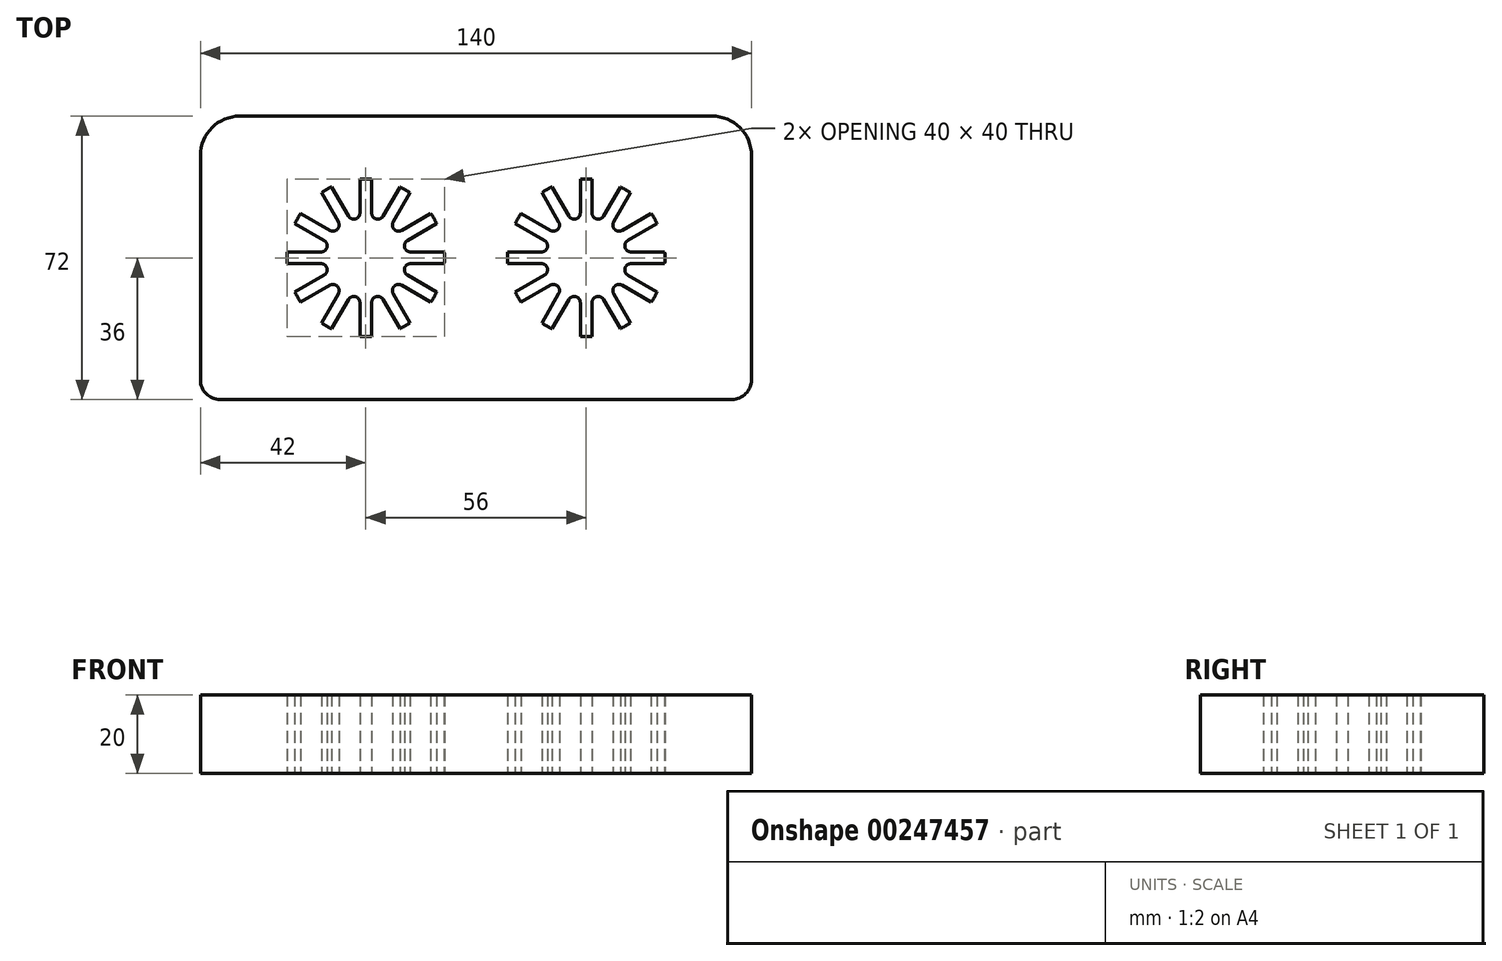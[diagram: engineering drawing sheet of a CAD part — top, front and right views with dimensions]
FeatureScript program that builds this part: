
annotation { "Feature Type Name" : "Feature", "Feature Type Description" : "" }
export const myFeature = defineFeature(function(context is Context, id is Id, definition is map)
    precondition{}
    {
        {
            var Q0;
            Q0=qCreatedBy(makeId("Top.planeOp"),FACE);
            var sketch = newSketch(context, id + "F0", { "sketchPlane" : qUnion([Q0])});
            skArc(sketch, "E0", {"start": v(-16.52, 11.27) * mm, "mid": v(-17.32, 10) * mm, "end": v(-18.02, 8.67) * mm});
            skArc(sketch, "E1", {"start": v(-6.35, 8) * mm, "mid": v(-7.23, 7.23) * mm, "end": v(-8, 6.35) * mm});
            skLineSegment(sketch, "E2", {"start": v(-19.94, -1.5) * mm, "end": v(-10.1, -1.5) * mm});
            skLineSegment(sketch, "E3", {"start": v(-20, 1.5) * mm, "end": v(-10.1, 1.5) * mm});
            skLineSegment(sketch, "E4", {"start": v(-18.02, 8.67) * mm, "end": v(-9.5, 3.76) * mm});
            skLineSegment(sketch, "E5", {"start": v(-16.52, 11.27) * mm, "end": v(-8, 6.35) * mm});
            skLineSegment(sketch, "E6", {"start": v(-1.5, 19.94) * mm, "end": v(-1.5, 10.1) * mm});
            skLineSegment(sketch, "E7", {"start": v(1.5, 19.94) * mm, "end": v(1.5, 10.1) * mm});
            skLineSegment(sketch, "E8", {"start": v(-8.42, 17.58) * mm, "end": v(-8.67, 18.02) * mm});
            skLineSegment(sketch, "E9", {"start": v(-8.67, 18.02) * mm, "end": v(-3.76, 9.5) * mm});
            skLineSegment(sketch, "E10", {"start": v(10.76, 15.64) * mm, "end": v(11.27, 16.52) * mm});
            skLineSegment(sketch, "E11", {"start": v(11.27, 16.52) * mm, "end": v(6.35, 8) * mm});
            skLineSegment(sketch, "E12", {"start": v(8.17, 17.14) * mm, "end": v(8.67, 18.02) * mm});
            skLineSegment(sketch, "E13", {"start": v(8.67, 18.02) * mm, "end": v(3.76, 9.5) * mm});
            skLineSegment(sketch, "E14", {"start": v(17.6, 8.43) * mm, "end": v(18.02, 8.67) * mm});
            skLineSegment(sketch, "E15", {"start": v(18.02, 8.67) * mm, "end": v(9.5, 3.76) * mm});
            skLineSegment(sketch, "E16", {"start": v(16.1, 11.03) * mm, "end": v(16.52, 11.27) * mm});
            skLineSegment(sketch, "E17", {"start": v(16.52, 11.27) * mm, "end": v(8, 6.35) * mm});
            skLineSegment(sketch, "E18", {"start": v(-10.8, 15.7) * mm, "end": v(-11.27, 16.52) * mm});
            skLineSegment(sketch, "E19", {"start": v(-10.8, 15.7) * mm, "end": v(-6.35, 8) * mm});
            skLineSegment(sketch, "E20.trimOffspring", {"start": v(-9.5, -3.76) * mm, "end": v(-18.02, -8.67) * mm});
            skLineSegment(sketch, "E21.trimOffspring", {"start": v(-8, -6.35) * mm, "end": v(-16.52, -11.27) * mm});
            skLineSegment(sketch, "E22.trimOffspring", {"start": v(-6.35, -8) * mm, "end": v(-11.27, -16.52) * mm});
            skLineSegment(sketch, "E23.trimOffspring", {"start": v(-3.76, -9.5) * mm, "end": v(-8.67, -18.02) * mm});
            skLineSegment(sketch, "E24.trimOffspring", {"start": v(-1.5, -10.1) * mm, "end": v(-1.5, -19.94) * mm});
            skLineSegment(sketch, "E25.trimOffspring", {"start": v(1.5, -10.1) * mm, "end": v(1.5, -19.94) * mm});
            skLineSegment(sketch, "E26.trimOffspring", {"start": v(3.76, -9.5) * mm, "end": v(8.67, -18.02) * mm});
            skLineSegment(sketch, "E27.trimOffspring", {"start": v(6.35, -8) * mm, "end": v(11.27, -16.52) * mm});
            skLineSegment(sketch, "E28.trimOffspring", {"start": v(8, -6.35) * mm, "end": v(16.52, -11.27) * mm});
            skLineSegment(sketch, "E29.trimOffspring", {"start": v(9.5, -3.76) * mm, "end": v(18.02, -8.67) * mm});
            skLineSegment(sketch, "E30.trimOffspring", {"start": v(10.1, -1.5) * mm, "end": v(19.94, -1.5) * mm});
            skLineSegment(sketch, "E31.trimOffspring", {"start": v(10.1, 1.5) * mm, "end": v(19.94, 1.5) * mm});
            skLineSegment(sketch, "E32", {"start": v(0, 0) * mm, "end": v(0, 20) * mm, "construction": true});
            skLineSegment(sketch, "E33", {"start": v(0, 0) * mm, "end": v(10, 17.32) * mm, "construction": true});
            skLineSegment(sketch, "E34", {"start": v(0, 0) * mm, "end": v(17.32, 10) * mm, "construction": true});
            skLineSegment(sketch, "E35", {"start": v(0, 0) * mm, "end": v(20, 0) * mm, "construction": true});
            skLineSegment(sketch, "E36", {"start": v(0, 0) * mm, "end": v(17.32, -10) * mm, "construction": true});
            skLineSegment(sketch, "E37", {"start": v(0, 0) * mm, "end": v(10, -17.32) * mm, "construction": true});
            skLineSegment(sketch, "E38", {"start": v(0, 0) * mm, "end": v(0, -20) * mm, "construction": true});
            skLineSegment(sketch, "E39", {"start": v(0, 0) * mm, "end": v(-10, -17.32) * mm, "construction": true});
            skLineSegment(sketch, "E40", {"start": v(0, 0) * mm, "end": v(-20, 0) * mm, "construction": true});
            skLineSegment(sketch, "E41", {"start": v(0, 0) * mm, "end": v(-17.32, 10) * mm, "construction": true});
            skLineSegment(sketch, "E42", {"start": v(0, 0) * mm, "end": v(-10, 17.32) * mm, "construction": true});
            skLineSegment(sketch, "E43", {"start": v(0, 0) * mm, "end": v(-17.32, -10) * mm, "construction": true});
            skArc(sketch, "E44.trimOffspring", {"start": v(-1.5, 10.1) * mm, "mid": v(-2.65, 9.87) * mm, "end": v(-3.76, 9.5) * mm});
            skArc(sketch, "E45.trimOffspring", {"start": v(3.76, 9.5) * mm, "mid": v(2.65, 9.87) * mm, "end": v(1.5, 10.1) * mm});
            skArc(sketch, "E46.trimOffspring", {"start": v(8, 6.35) * mm, "mid": v(7.23, 7.23) * mm, "end": v(6.35, 8) * mm});
            skArc(sketch, "E47.trimOffspring", {"start": v(10.1, 1.5) * mm, "mid": v(9.87, 2.65) * mm, "end": v(9.5, 3.76) * mm});
            skArc(sketch, "E48.trimOffspring", {"start": v(9.5, -3.76) * mm, "mid": v(9.87, -2.65) * mm, "end": v(10.1, -1.5) * mm});
            skArc(sketch, "E49.trimOffspring", {"start": v(6.35, -8) * mm, "mid": v(7.23, -7.23) * mm, "end": v(8, -6.35) * mm});
            skArc(sketch, "E50.trimOffspring", {"start": v(1.5, -10.1) * mm, "mid": v(2.65, -9.87) * mm, "end": v(3.76, -9.5) * mm});
            skArc(sketch, "E51.trimOffspring", {"start": v(-3.76, -9.5) * mm, "mid": v(-2.65, -9.87) * mm, "end": v(-1.5, -10.1) * mm});
            skArc(sketch, "E52.trimOffspring", {"start": v(-8, -6.35) * mm, "mid": v(-7.23, -7.23) * mm, "end": v(-6.35, -8) * mm});
            skArc(sketch, "E53.trimOffspring", {"start": v(-10.1, -1.5) * mm, "mid": v(-9.87, -2.65) * mm, "end": v(-9.5, -3.76) * mm});
            skArc(sketch, "E54.trimOffspring", {"start": v(-9.5, 3.76) * mm, "mid": v(-9.87, 2.65) * mm, "end": v(-10.1, 1.5) * mm});
            skArc(sketch, "E55.trimOffspring", {"start": v(-8.67, 18.02) * mm, "mid": v(-10, 17.32) * mm, "end": v(-11.27, 16.52) * mm});
            skArc(sketch, "E56.trimOffspring", {"start": v(1.5, 19.94) * mm, "mid": v(0, 20) * mm, "end": v(-1.5, 19.94) * mm});
            skArc(sketch, "E57.trimOffspring", {"start": v(11.27, 16.52) * mm, "mid": v(10, 17.32) * mm, "end": v(8.67, 18.02) * mm});
            skArc(sketch, "E58.trimOffspring", {"start": v(18.02, 8.67) * mm, "mid": v(17.32, 10) * mm, "end": v(16.52, 11.27) * mm});
            skArc(sketch, "E59.trimOffspring", {"start": v(19.94, -1.5) * mm, "mid": v(20, 0) * mm, "end": v(19.94, 1.5) * mm});
            skArc(sketch, "E60.trimOffspring", {"start": v(16.52, -11.27) * mm, "mid": v(17.32, -10) * mm, "end": v(18.02, -8.67) * mm});
            skArc(sketch, "E61.trimOffspring", {"start": v(8.67, -18.02) * mm, "mid": v(10, -17.32) * mm, "end": v(11.27, -16.52) * mm});
            skArc(sketch, "E62.trimOffspring", {"start": v(-1.5, -19.94) * mm, "mid": v(0, -20) * mm, "end": v(1.5, -19.94) * mm});
            skArc(sketch, "E63.trimOffspring", {"start": v(-11.27, -16.52) * mm, "mid": v(-10, -17.32) * mm, "end": v(-8.67, -18.02) * mm});
            skArc(sketch, "E64.trimOffspring", {"start": v(-18.02, -8.67) * mm, "mid": v(-17.32, -10) * mm, "end": v(-16.52, -11.27) * mm});
            skArc(sketch, "E65.trimOffspring", {"start": v(-19.94, 1.5) * mm, "mid": v(-20, 0) * mm, "end": v(-19.94, -1.5) * mm});
            skArc(sketch, "E66", {"start": v(-72.52, 11.27) * mm, "mid": v(-73.32, 10) * mm, "end": v(-74.02, 8.67) * mm});
            skArc(sketch, "E67", {"start": v(-62.35, 8) * mm, "mid": v(-63.23, 7.23) * mm, "end": v(-64, 6.35) * mm});
            skLineSegment(sketch, "E68", {"start": v(-75.94, -1.5) * mm, "end": v(-66.1, -1.5) * mm});
            skLineSegment(sketch, "E69", {"start": v(-76, 1.5) * mm, "end": v(-66.1, 1.5) * mm});
            skLineSegment(sketch, "E70", {"start": v(-74.02, 8.67) * mm, "end": v(-65.5, 3.76) * mm});
            skLineSegment(sketch, "E71", {"start": v(-72.52, 11.27) * mm, "end": v(-64, 6.35) * mm});
            skLineSegment(sketch, "E72", {"start": v(-57.5, 19.94) * mm, "end": v(-57.5, 10.1) * mm});
            skLineSegment(sketch, "E73", {"start": v(-54.5, 19.94) * mm, "end": v(-54.5, 10.1) * mm});
            skLineSegment(sketch, "E74", {"start": v(-64.42, 17.58) * mm, "end": v(-64.67, 18.02) * mm});
            skLineSegment(sketch, "E75", {"start": v(-64.67, 18.02) * mm, "end": v(-59.76, 9.5) * mm});
            skLineSegment(sketch, "E76", {"start": v(-45.24, 15.64) * mm, "end": v(-44.73, 16.52) * mm});
            skLineSegment(sketch, "E77", {"start": v(-44.73, 16.52) * mm, "end": v(-49.65, 8) * mm});
            skLineSegment(sketch, "E78", {"start": v(-47.83, 17.14) * mm, "end": v(-47.33, 18.02) * mm});
            skLineSegment(sketch, "E79", {"start": v(-47.33, 18.02) * mm, "end": v(-52.24, 9.5) * mm});
            skLineSegment(sketch, "E80", {"start": v(-38.4, 8.43) * mm, "end": v(-37.98, 8.67) * mm});
            skLineSegment(sketch, "E81", {"start": v(-37.98, 8.67) * mm, "end": v(-46.5, 3.76) * mm});
            skLineSegment(sketch, "E82", {"start": v(-39.9, 11.03) * mm, "end": v(-39.48, 11.27) * mm});
            skLineSegment(sketch, "E83", {"start": v(-39.48, 11.27) * mm, "end": v(-48, 6.35) * mm});
            skLineSegment(sketch, "E84", {"start": v(-66.8, 15.7) * mm, "end": v(-67.27, 16.52) * mm});
            skLineSegment(sketch, "E85", {"start": v(-66.8, 15.7) * mm, "end": v(-62.35, 8) * mm});
            skLineSegment(sketch, "E86.trimOffspring", {"start": v(-65.5, -3.76) * mm, "end": v(-74.02, -8.67) * mm});
            skLineSegment(sketch, "E87.trimOffspring", {"start": v(-64, -6.35) * mm, "end": v(-72.52, -11.27) * mm});
            skLineSegment(sketch, "E88.trimOffspring", {"start": v(-62.35, -8) * mm, "end": v(-67.27, -16.52) * mm});
            skLineSegment(sketch, "E89.trimOffspring", {"start": v(-59.76, -9.5) * mm, "end": v(-64.67, -18.02) * mm});
            skLineSegment(sketch, "E90.trimOffspring", {"start": v(-57.5, -10.1) * mm, "end": v(-57.5, -19.94) * mm});
            skLineSegment(sketch, "E91.trimOffspring", {"start": v(-54.5, -10.1) * mm, "end": v(-54.5, -19.94) * mm});
            skLineSegment(sketch, "E92.trimOffspring", {"start": v(-52.24, -9.5) * mm, "end": v(-47.33, -18.02) * mm});
            skLineSegment(sketch, "E93.trimOffspring", {"start": v(-49.65, -8) * mm, "end": v(-44.73, -16.52) * mm});
            skLineSegment(sketch, "E94.trimOffspring", {"start": v(-48, -6.35) * mm, "end": v(-39.48, -11.27) * mm});
            skLineSegment(sketch, "E95.trimOffspring", {"start": v(-46.5, -3.76) * mm, "end": v(-37.98, -8.67) * mm});
            skLineSegment(sketch, "E96.trimOffspring", {"start": v(-45.9, -1.5) * mm, "end": v(-36.06, -1.5) * mm});
            skLineSegment(sketch, "E97.trimOffspring", {"start": v(-45.9, 1.5) * mm, "end": v(-36.06, 1.5) * mm});
            skLineSegment(sketch, "E98", {"start": v(-56, 0) * mm, "end": v(-56, 20) * mm, "construction": true});
            skLineSegment(sketch, "E99", {"start": v(-56, 0) * mm, "end": v(-46, 17.32) * mm, "construction": true});
            skLineSegment(sketch, "E100", {"start": v(-56, 0) * mm, "end": v(-38.68, 10) * mm, "construction": true});
            skLineSegment(sketch, "E101", {"start": v(-56, 0) * mm, "end": v(-36, 0) * mm, "construction": true});
            skLineSegment(sketch, "E102", {"start": v(-56, 0) * mm, "end": v(-38.68, -10) * mm, "construction": true});
            skLineSegment(sketch, "E103", {"start": v(-56, 0) * mm, "end": v(-46, -17.32) * mm, "construction": true});
            skLineSegment(sketch, "E104", {"start": v(-56, 0) * mm, "end": v(-56, -20) * mm, "construction": true});
            skLineSegment(sketch, "E105", {"start": v(-56, 0) * mm, "end": v(-66, -17.32) * mm, "construction": true});
            skLineSegment(sketch, "E106", {"start": v(-56, 0) * mm, "end": v(-76, 0) * mm, "construction": true});
            skLineSegment(sketch, "E107", {"start": v(-56, 0) * mm, "end": v(-73.32, 10) * mm, "construction": true});
            skLineSegment(sketch, "E108", {"start": v(-56, 0) * mm, "end": v(-66, 17.32) * mm, "construction": true});
            skLineSegment(sketch, "E109", {"start": v(-56, 0) * mm, "end": v(-73.32, -10) * mm, "construction": true});
            skArc(sketch, "E110.trimOffspring", {"start": v(-57.5, 10.1) * mm, "mid": v(-58.65, 9.87) * mm, "end": v(-59.76, 9.5) * mm});
            skArc(sketch, "E111.trimOffspring", {"start": v(-52.24, 9.5) * mm, "mid": v(-53.35, 9.87) * mm, "end": v(-54.5, 10.1) * mm});
            skArc(sketch, "E112.trimOffspring", {"start": v(-48, 6.35) * mm, "mid": v(-48.77, 7.23) * mm, "end": v(-49.65, 8) * mm});
            skArc(sketch, "E113.trimOffspring", {"start": v(-45.9, 1.5) * mm, "mid": v(-46.13, 2.65) * mm, "end": v(-46.5, 3.76) * mm});
            skArc(sketch, "E114.trimOffspring", {"start": v(-46.5, -3.76) * mm, "mid": v(-46.13, -2.65) * mm, "end": v(-45.9, -1.5) * mm});
            skArc(sketch, "E115.trimOffspring", {"start": v(-49.65, -8) * mm, "mid": v(-48.77, -7.23) * mm, "end": v(-48, -6.35) * mm});
            skArc(sketch, "E116.trimOffspring", {"start": v(-54.5, -10.1) * mm, "mid": v(-53.35, -9.87) * mm, "end": v(-52.24, -9.5) * mm});
            skArc(sketch, "E117.trimOffspring", {"start": v(-59.76, -9.5) * mm, "mid": v(-58.65, -9.87) * mm, "end": v(-57.5, -10.1) * mm});
            skArc(sketch, "E118.trimOffspring", {"start": v(-64, -6.35) * mm, "mid": v(-63.23, -7.23) * mm, "end": v(-62.35, -8) * mm});
            skArc(sketch, "E119.trimOffspring", {"start": v(-66.1, -1.5) * mm, "mid": v(-65.87, -2.65) * mm, "end": v(-65.5, -3.76) * mm});
            skArc(sketch, "E120.trimOffspring", {"start": v(-65.5, 3.76) * mm, "mid": v(-65.87, 2.65) * mm, "end": v(-66.1, 1.5) * mm});
            skArc(sketch, "E121.trimOffspring", {"start": v(-64.67, 18.02) * mm, "mid": v(-66, 17.32) * mm, "end": v(-67.27, 16.52) * mm});
            skArc(sketch, "E122.trimOffspring", {"start": v(-54.5, 19.94) * mm, "mid": v(-56, 20) * mm, "end": v(-57.5, 19.94) * mm});
            skArc(sketch, "E123.trimOffspring", {"start": v(-44.73, 16.52) * mm, "mid": v(-46, 17.32) * mm, "end": v(-47.33, 18.02) * mm});
            skArc(sketch, "E124.trimOffspring", {"start": v(-37.98, 8.67) * mm, "mid": v(-38.68, 10) * mm, "end": v(-39.48, 11.27) * mm});
            skArc(sketch, "E125.trimOffspring", {"start": v(-36.06, -1.5) * mm, "mid": v(-36, 0) * mm, "end": v(-36.06, 1.5) * mm});
            skArc(sketch, "E126.trimOffspring", {"start": v(-39.48, -11.27) * mm, "mid": v(-38.68, -10) * mm, "end": v(-37.98, -8.67) * mm});
            skArc(sketch, "E127.trimOffspring", {"start": v(-47.33, -18.02) * mm, "mid": v(-46, -17.32) * mm, "end": v(-44.73, -16.52) * mm});
            skArc(sketch, "E128.trimOffspring", {"start": v(-57.5, -19.94) * mm, "mid": v(-56, -20) * mm, "end": v(-54.5, -19.94) * mm});
            skArc(sketch, "E129.trimOffspring", {"start": v(-67.27, -16.52) * mm, "mid": v(-66, -17.32) * mm, "end": v(-64.67, -18.02) * mm});
            skArc(sketch, "E130.trimOffspring", {"start": v(-74.02, -8.67) * mm, "mid": v(-73.32, -10) * mm, "end": v(-72.52, -11.27) * mm});
            skArc(sketch, "E131.trimOffspring", {"start": v(-75.94, 1.5) * mm, "mid": v(-76, 0) * mm, "end": v(-75.94, -1.5) * mm});
            skLineSegment(sketch, "E132", {"start": v(42, -31) * mm, "end": v(42, 26) * mm});
            skLineSegment(sketch, "E133", {"start": v(32, 36) * mm, "end": v(-88, 36) * mm});
            skLineSegment(sketch, "E134", {"start": v(-98, 26) * mm, "end": v(-98, -31) * mm});
            skPoint(sketch, "E135.visualSharp", {"position": v(-98, 36) * mm});
            skArc(sketch, "E135.filletArc", {"start": v(-88, 36) * mm, "mid": v(-95.07, 33.07) * mm, "end": v(-98, 26) * mm});
            skPoint(sketch, "E136.visualSharp", {"position": v(42, 36) * mm});
            skArc(sketch, "E136.filletArc", {"start": v(42, 26) * mm, "mid": v(39.07, 33.07) * mm, "end": v(32, 36) * mm});
            skPoint(sketch, "E137.visualSharp", {"position": v(-98, -36) * mm});
            skArc(sketch, "E137.filletArc", {"start": v(-98, -31) * mm, "mid": v(-96.54, -34.54) * mm, "end": v(-93, -36) * mm});
            skPoint(sketch, "E138.visualSharp", {"position": v(42, -36) * mm});
            skArc(sketch, "E138.filletArc", {"start": v(37, -36) * mm, "mid": v(40.54, -34.54) * mm, "end": v(42, -31) * mm});
            skLineSegment(sketch, "E139", {"start": v(-93, -36) * mm, "end": v(37, -36) * mm});
            skSolve(sketch);
        }
        {
            var Q0;
            Q0 = qSketchRegion(id + "F0", true);
            extrude(context, id + "F1", {"entities" : qUnion([Q0]), "depth" : 20 * mm});
        }
        {
            var Q0;
            Q0=makeQuery(id+"F1.opExtrude","SWEPT_EDGE",EDGE,{"disambiguationData":[OSD([sQuery(id+"F0.wireOp",EDGE,"E9"),sQuery(id+"F0.wireOp",EDGE,"E44.trimOffspring")])]});
            var Q1;
            Q1=makeQuery(id+"F1.opExtrude","SWEPT_EDGE",EDGE,{"disambiguationData":[OSD([sQuery(id+"F0.wireOp",EDGE,"E6"),sQuery(id+"F0.wireOp",EDGE,"E44.trimOffspring")])]});
            var Q2;
            Q2=makeQuery(id+"F1.opExtrude","SWEPT_EDGE",EDGE,{"disambiguationData":[OSD([sQuery(id+"F0.wireOp",EDGE,"E13"),sQuery(id+"F0.wireOp",EDGE,"E45.trimOffspring")])]});
            var Q3;
            Q3=makeQuery(id+"F1.opExtrude","SWEPT_EDGE",EDGE,{"disambiguationData":[OSD([sQuery(id+"F0.wireOp",EDGE,"E7"),sQuery(id+"F0.wireOp",EDGE,"E45.trimOffspring")])]});
            var Q4;
            Q4=makeQuery(id+"F1.opExtrude","SWEPT_EDGE",EDGE,{"disambiguationData":[OSD([sQuery(id+"F0.wireOp",EDGE,"E11"),sQuery(id+"F0.wireOp",EDGE,"E46.trimOffspring")])]});
            var Q5;
            Q5=makeQuery(id+"F1.opExtrude","SWEPT_EDGE",EDGE,{"disambiguationData":[OSD([sQuery(id+"F0.wireOp",EDGE,"E17"),sQuery(id+"F0.wireOp",EDGE,"E46.trimOffspring")])]});
            var Q6;
            Q6=makeQuery(id+"F1.opExtrude","SWEPT_EDGE",EDGE,{"disambiguationData":[OSD([sQuery(id+"F0.wireOp",EDGE,"E15"),sQuery(id+"F0.wireOp",EDGE,"E47.trimOffspring")])]});
            var Q7;
            Q7=makeQuery(id+"F1.opExtrude","SWEPT_EDGE",EDGE,{"disambiguationData":[OSD([sQuery(id+"F0.wireOp",EDGE,"E31.trimOffspring"),sQuery(id+"F0.wireOp",EDGE,"E47.trimOffspring")])]});
            var Q8;
            Q8=makeQuery(id+"F1.opExtrude","SWEPT_EDGE",EDGE,{"disambiguationData":[OSD([sQuery(id+"F0.wireOp",EDGE,"E30.trimOffspring"),sQuery(id+"F0.wireOp",EDGE,"E48.trimOffspring")])]});
            var Q9;
            Q9=makeQuery(id+"F1.opExtrude","SWEPT_EDGE",EDGE,{"disambiguationData":[OSD([sQuery(id+"F0.wireOp",EDGE,"E29.trimOffspring"),sQuery(id+"F0.wireOp",EDGE,"E48.trimOffspring")])]});
            var Q10;
            Q10=makeQuery(id+"F1.opExtrude","SWEPT_EDGE",EDGE,{"disambiguationData":[OSD([sQuery(id+"F0.wireOp",EDGE,"E28.trimOffspring"),sQuery(id+"F0.wireOp",EDGE,"E49.trimOffspring")])]});
            var Q11;
            Q11=makeQuery(id+"F1.opExtrude","SWEPT_EDGE",EDGE,{"disambiguationData":[OSD([sQuery(id+"F0.wireOp",EDGE,"E27.trimOffspring"),sQuery(id+"F0.wireOp",EDGE,"E49.trimOffspring")])]});
            var Q12;
            Q12=makeQuery(id+"F1.opExtrude","SWEPT_EDGE",EDGE,{"disambiguationData":[OSD([sQuery(id+"F0.wireOp",EDGE,"E26.trimOffspring"),sQuery(id+"F0.wireOp",EDGE,"E50.trimOffspring")])]});
            var Q13;
            Q13=makeQuery(id+"F1.opExtrude","SWEPT_EDGE",EDGE,{"disambiguationData":[OSD([sQuery(id+"F0.wireOp",EDGE,"E25.trimOffspring"),sQuery(id+"F0.wireOp",EDGE,"E50.trimOffspring")])]});
            var Q14;
            Q14=makeQuery(id+"F1.opExtrude","SWEPT_EDGE",EDGE,{"disambiguationData":[OSD([sQuery(id+"F0.wireOp",EDGE,"E23.trimOffspring"),sQuery(id+"F0.wireOp",EDGE,"E51.trimOffspring")])]});
            var Q15;
            Q15=makeQuery(id+"F1.opExtrude","SWEPT_EDGE",EDGE,{"disambiguationData":[OSD([sQuery(id+"F0.wireOp",EDGE,"E24.trimOffspring"),sQuery(id+"F0.wireOp",EDGE,"E51.trimOffspring")])]});
            var Q16;
            Q16=makeQuery(id+"F1.opExtrude","SWEPT_EDGE",EDGE,{"disambiguationData":[OSD([sQuery(id+"F0.wireOp",EDGE,"E21.trimOffspring"),sQuery(id+"F0.wireOp",EDGE,"E52.trimOffspring")])]});
            var Q17;
            Q17=makeQuery(id+"F1.opExtrude","SWEPT_EDGE",EDGE,{"disambiguationData":[OSD([sQuery(id+"F0.wireOp",EDGE,"E22.trimOffspring"),sQuery(id+"F0.wireOp",EDGE,"E52.trimOffspring")])]});
            var Q18;
            Q18=makeQuery(id+"F1.opExtrude","SWEPT_EDGE",EDGE,{"disambiguationData":[OSD([sQuery(id+"F0.wireOp",EDGE,"E2"),sQuery(id+"F0.wireOp",EDGE,"E53.trimOffspring")])]});
            var Q19;
            Q19=makeQuery(id+"F1.opExtrude","SWEPT_EDGE",EDGE,{"disambiguationData":[OSD([sQuery(id+"F0.wireOp",EDGE,"E20.trimOffspring"),sQuery(id+"F0.wireOp",EDGE,"E53.trimOffspring")])]});
            var Q20;
            Q20=makeQuery(id+"F1.opExtrude","SWEPT_EDGE",EDGE,{"disambiguationData":[OSD([sQuery(id+"F0.wireOp",EDGE,"E4"),sQuery(id+"F0.wireOp",EDGE,"E54.trimOffspring")])]});
            var Q21;
            Q21=makeQuery(id+"F1.opExtrude","SWEPT_EDGE",EDGE,{"disambiguationData":[OSD([sQuery(id+"F0.wireOp",EDGE,"E3"),sQuery(id+"F0.wireOp",EDGE,"E54.trimOffspring")])]});
            var Q22;
            Q22=makeQuery(id+"F1.opExtrude","SWEPT_EDGE",EDGE,{"disambiguationData":[OSD([sQuery(id+"F0.wireOp",EDGE,"E67"),sQuery(id+"F0.wireOp",EDGE,"E85")])]});
            var Q23;
            Q23=makeQuery(id+"F1.opExtrude","SWEPT_EDGE",EDGE,{"disambiguationData":[OSD([sQuery(id+"F0.wireOp",EDGE,"E67"),sQuery(id+"F0.wireOp",EDGE,"E71")])]});
            var Q24;
            Q24=makeQuery(id+"F1.opExtrude","SWEPT_EDGE",EDGE,{"disambiguationData":[OSD([sQuery(id+"F0.wireOp",EDGE,"E75"),sQuery(id+"F0.wireOp",EDGE,"E110.trimOffspring")])]});
            var Q25;
            Q25=makeQuery(id+"F1.opExtrude","SWEPT_EDGE",EDGE,{"disambiguationData":[OSD([sQuery(id+"F0.wireOp",EDGE,"E72"),sQuery(id+"F0.wireOp",EDGE,"E110.trimOffspring")])]});
            var Q26;
            Q26=makeQuery(id+"F1.opExtrude","SWEPT_EDGE",EDGE,{"disambiguationData":[OSD([sQuery(id+"F0.wireOp",EDGE,"E79"),sQuery(id+"F0.wireOp",EDGE,"E111.trimOffspring")])]});
            var Q27;
            Q27=makeQuery(id+"F1.opExtrude","SWEPT_EDGE",EDGE,{"disambiguationData":[OSD([sQuery(id+"F0.wireOp",EDGE,"E83"),sQuery(id+"F0.wireOp",EDGE,"E112.trimOffspring")])]});
            var Q28;
            Q28=makeQuery(id+"F1.opExtrude","SWEPT_EDGE",EDGE,{"disambiguationData":[OSD([sQuery(id+"F0.wireOp",EDGE,"E73"),sQuery(id+"F0.wireOp",EDGE,"E111.trimOffspring")])]});
            var Q29;
            Q29=makeQuery(id+"F1.opExtrude","SWEPT_EDGE",EDGE,{"disambiguationData":[OSD([sQuery(id+"F0.wireOp",EDGE,"E77"),sQuery(id+"F0.wireOp",EDGE,"E112.trimOffspring")])]});
            var Q30;
            Q30=makeQuery(id+"F1.opExtrude","SWEPT_EDGE",EDGE,{"disambiguationData":[OSD([sQuery(id+"F0.wireOp",EDGE,"E97.trimOffspring"),sQuery(id+"F0.wireOp",EDGE,"E113.trimOffspring")])]});
            var Q31;
            Q31=makeQuery(id+"F1.opExtrude","SWEPT_EDGE",EDGE,{"disambiguationData":[OSD([sQuery(id+"F0.wireOp",EDGE,"E81"),sQuery(id+"F0.wireOp",EDGE,"E113.trimOffspring")])]});
            var Q32;
            Q32=makeQuery(id+"F1.opExtrude","SWEPT_EDGE",EDGE,{"disambiguationData":[OSD([sQuery(id+"F0.wireOp",EDGE,"E70"),sQuery(id+"F0.wireOp",EDGE,"E120.trimOffspring")])]});
            var Q33;
            Q33=makeQuery(id+"F1.opExtrude","SWEPT_EDGE",EDGE,{"disambiguationData":[OSD([sQuery(id+"F0.wireOp",EDGE,"E86.trimOffspring"),sQuery(id+"F0.wireOp",EDGE,"E119.trimOffspring")])]});
            var Q34;
            Q34=makeQuery(id+"F1.opExtrude","SWEPT_EDGE",EDGE,{"disambiguationData":[OSD([sQuery(id+"F0.wireOp",EDGE,"E68"),sQuery(id+"F0.wireOp",EDGE,"E119.trimOffspring")])]});
            var Q35;
            Q35=makeQuery(id+"F1.opExtrude","SWEPT_EDGE",EDGE,{"disambiguationData":[OSD([sQuery(id+"F0.wireOp",EDGE,"E69"),sQuery(id+"F0.wireOp",EDGE,"E120.trimOffspring")])]});
            var Q36;
            Q36=makeQuery(id+"F1.opExtrude","SWEPT_EDGE",EDGE,{"disambiguationData":[OSD([sQuery(id+"F0.wireOp",EDGE,"E87.trimOffspring"),sQuery(id+"F0.wireOp",EDGE,"E118.trimOffspring")])]});
            var Q37;
            Q37=makeQuery(id+"F1.opExtrude","SWEPT_EDGE",EDGE,{"disambiguationData":[OSD([sQuery(id+"F0.wireOp",EDGE,"E88.trimOffspring"),sQuery(id+"F0.wireOp",EDGE,"E118.trimOffspring")])]});
            var Q38;
            Q38=makeQuery(id+"F1.opExtrude","SWEPT_EDGE",EDGE,{"disambiguationData":[OSD([sQuery(id+"F0.wireOp",EDGE,"E89.trimOffspring"),sQuery(id+"F0.wireOp",EDGE,"E117.trimOffspring")])]});
            var Q39;
            Q39=makeQuery(id+"F1.opExtrude","SWEPT_EDGE",EDGE,{"disambiguationData":[OSD([sQuery(id+"F0.wireOp",EDGE,"E90.trimOffspring"),sQuery(id+"F0.wireOp",EDGE,"E117.trimOffspring")])]});
            var Q40;
            Q40=makeQuery(id+"F1.opExtrude","SWEPT_EDGE",EDGE,{"disambiguationData":[OSD([sQuery(id+"F0.wireOp",EDGE,"E92.trimOffspring"),sQuery(id+"F0.wireOp",EDGE,"E116.trimOffspring")])]});
            var Q41;
            Q41=makeQuery(id+"F1.opExtrude","SWEPT_EDGE",EDGE,{"disambiguationData":[OSD([sQuery(id+"F0.wireOp",EDGE,"E91.trimOffspring"),sQuery(id+"F0.wireOp",EDGE,"E116.trimOffspring")])]});
            var Q42;
            Q42=makeQuery(id+"F1.opExtrude","SWEPT_EDGE",EDGE,{"disambiguationData":[OSD([sQuery(id+"F0.wireOp",EDGE,"E93.trimOffspring"),sQuery(id+"F0.wireOp",EDGE,"E115.trimOffspring")])]});
            var Q43;
            Q43=makeQuery(id+"F1.opExtrude","SWEPT_EDGE",EDGE,{"disambiguationData":[OSD([sQuery(id+"F0.wireOp",EDGE,"E94.trimOffspring"),sQuery(id+"F0.wireOp",EDGE,"E115.trimOffspring")])]});
            var Q44;
            Q44=makeQuery(id+"F1.opExtrude","SWEPT_EDGE",EDGE,{"disambiguationData":[OSD([sQuery(id+"F0.wireOp",EDGE,"E95.trimOffspring"),sQuery(id+"F0.wireOp",EDGE,"E114.trimOffspring")])]});
            var Q45;
            Q45=makeQuery(id+"F1.opExtrude","SWEPT_EDGE",EDGE,{"disambiguationData":[OSD([sQuery(id+"F0.wireOp",EDGE,"E96.trimOffspring"),sQuery(id+"F0.wireOp",EDGE,"E114.trimOffspring")])]});
            var Q46;
            Q46=makeQuery(id+"F1.opExtrude","SWEPT_EDGE",EDGE,{"disambiguationData":[OSD([sQuery(id+"F0.wireOp",EDGE,"E1"),sQuery(id+"F0.wireOp",EDGE,"E19")])]});
            var Q47;
            Q47=makeQuery(id+"F1.opExtrude","SWEPT_EDGE",EDGE,{"disambiguationData":[OSD([sQuery(id+"F0.wireOp",EDGE,"E1"),sQuery(id+"F0.wireOp",EDGE,"E5")])]});
            fillet(context, id + "F2", {"entities" : qUnion([Q0, Q1, Q2, Q3, Q4, Q5, Q6, Q7, Q8, Q9, Q10, Q11, Q12, Q13, Q14, Q15, Q16, Q17, Q18, Q19, Q20, Q21, Q22, Q23, Q24, Q25, Q26, Q27, Q28, Q29, Q30, Q31, Q32, Q33, Q34, Q35, Q36, Q37, Q38, Q39, Q40, Q41, Q42, Q43, Q44, Q45, Q46, Q47]), "radius" : 1.5 * mm, "tangentPropagation" : true, "allowEdgeOverflow" : false});
        }
    });
